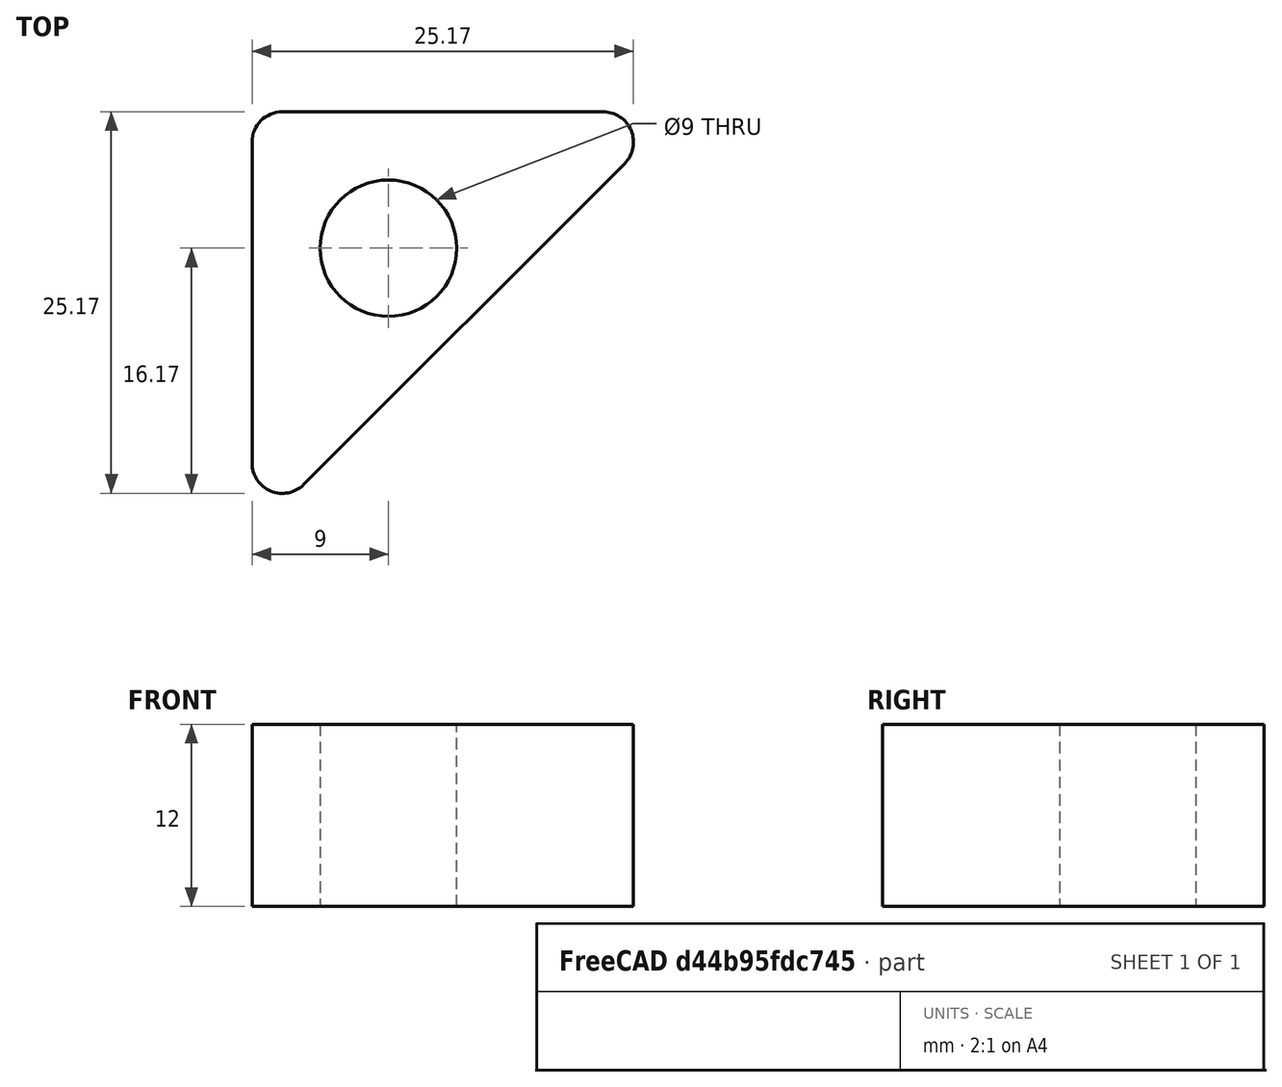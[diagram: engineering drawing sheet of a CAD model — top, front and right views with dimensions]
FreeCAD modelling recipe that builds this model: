
FCSTD DOCUMENT  (FreeCAD 0.19R24366 (Git))
Label: 12mm spacer for diagonal brace
License: All rights reserved
LicenseURL: http://en.wikipedia.org/wiki/All_rights_reserved
objects: Sketcher::SketchObject×1, PartDesign::Pad×1, PartDesign::Body×1
note: 4 computed .brp shape members not serialized (recipe doc carries the construction recipe); baked Part::Feature solids carry a one-line shape summary decoded from their .brp

FEATURE [Sketcher::SketchObject] Sketch
  FullyConstrained = true
  MapMode = 5
  Support = -> [XY_Plane]
  sketch-geometry (9):
    g0: LineSegment StartX=0 StartY=-2 StartZ=0 EndX=0 EndY=-23.1716 EndZ=0
    g1: LineSegment StartX=3.41421 StartY=-24.5858 StartZ=0 EndX=24.5858 EndY=-3.41421 EndZ=0
    g2: LineSegment StartX=23.1716 StartY=0 StartZ=0 EndX=2 EndY=0 EndZ=0
    g3: Circle CenterX=9 CenterY=-9 CenterZ=0 NormalX=0 NormalY=0 NormalZ=1 AngleXU=0 Radius=4.5
    g4: ArcOfCircle CenterX=2 CenterY=-23.1716 CenterZ=0 NormalX=0 NormalY=0 NormalZ=1 AngleXU=0 Radius=2 StartAngle=3.14159 EndAngle=5.49779
    g5: ArcOfCircle CenterX=2 CenterY=-2 CenterZ=0 NormalX=0 NormalY=0 NormalZ=1 AngleXU=0 Radius=2 StartAngle=1.5708 EndAngle=3.14159
    g6: ArcOfCircle CenterX=23.1716 CenterY=-2 CenterZ=0 NormalX=0 NormalY=0 NormalZ=1 AngleXU=0 Radius=2 StartAngle=5.49779 EndAngle=7.85398
    g7: LineSegment StartX=3.41421 StartY=-24.5858 StartZ=0 EndX=9e-16 EndY=-28 EndZ=0
    g8: LineSegment StartX=24.5858 StartY=-3.41421 StartZ=0 EndX=28 EndY=0 EndZ=0
  constraints (24):
    c: Equal(g2,g0)
    c: DistanceX(g-1,g3) = 9
    c: DistanceY(g3,g-1) = 9
    c: Radius(g3) = 4.5
    c: Tangent(g0,g4) = -1.5708
    c: Tangent(g1,g4) = -1.5708
    c: Tangent(g0,g5) = -1.5708
    c: Tangent(g2,g5) = -1.5708
    c: Tangent(g2,g6) = -1.5708
    c: Tangent(g1,g6) = -1.5708
    c: Horizontal(g2)
    c: Vertical(g0)
    c: PointOnObject(g0,g-2)
    c: PointOnObject(g2,g-1)
    c: Equal(g5,g4)
    c: Equal(g4,g6)
    c: Radius(g6) = 2
    c: Coincident(g7,g1)
    c: PointOnObject(g7,g-2)
    c: Coincident(g8,g1)
    c: PointOnObject(g8,g-1)
    c: Parallel(g1,g8)
    c: Parallel(g1,g7)
    c: DistanceY(g7,g-1) = 28
FEATURE [PartDesign::Pad] Pad
  Direction = (1,1,1)
  Length = 12
  Length2 = 100
  Profile = -> Sketch
  Type = 0
FEATURE [PartDesign::Body] Body
  Group = -> [Sketch,Pad]
  Origin = -> Origin
  Tip = -> Pad
